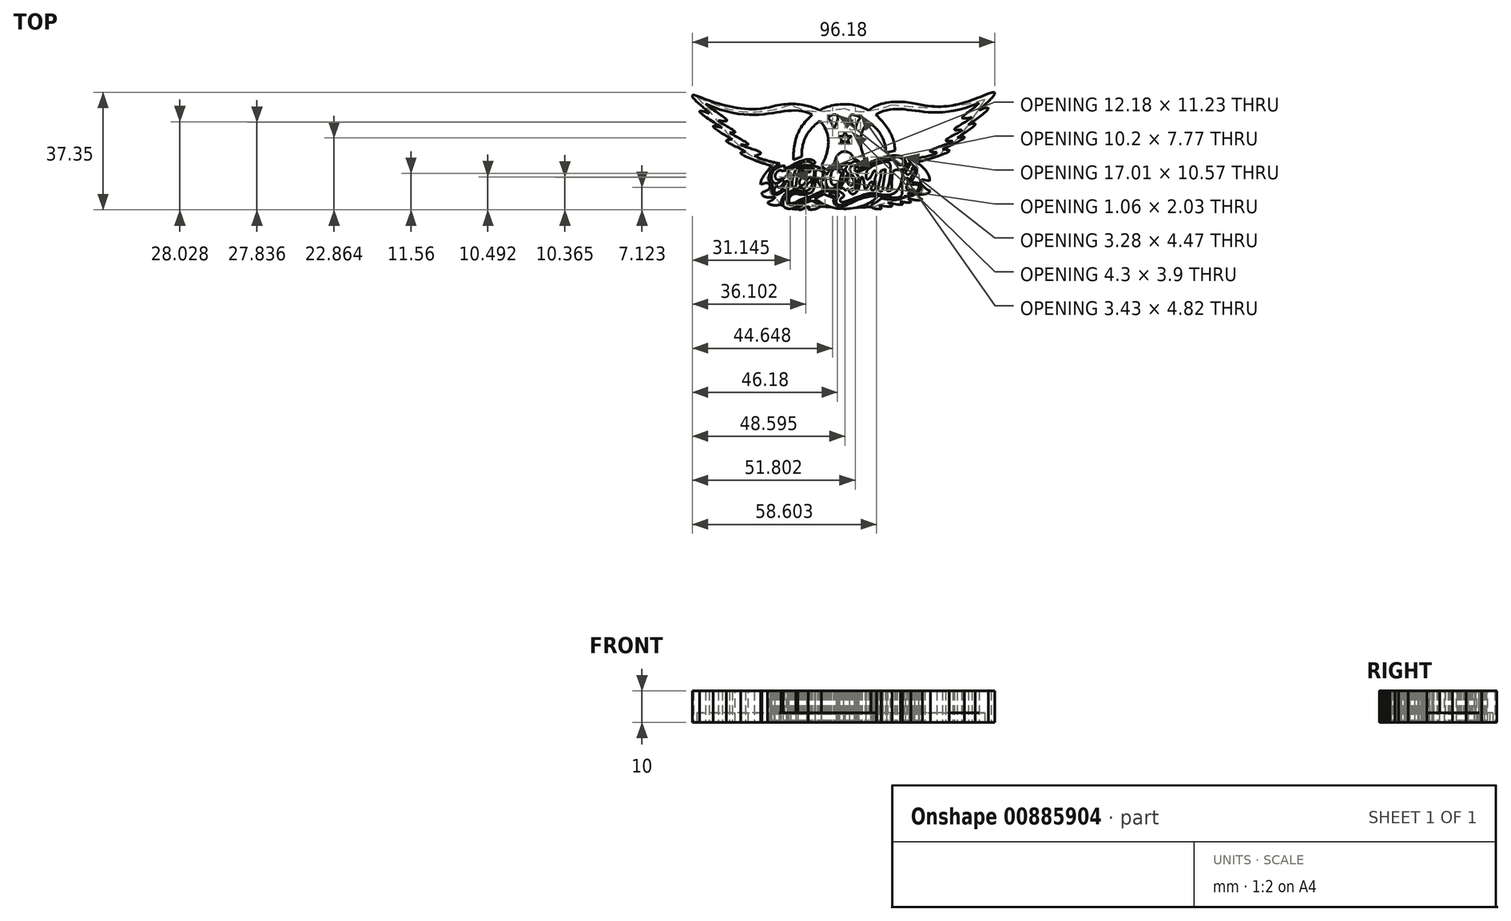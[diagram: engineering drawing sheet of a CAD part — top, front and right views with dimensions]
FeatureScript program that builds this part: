
annotation { "Feature Type Name" : "Feature", "Feature Type Description" : "" }
export const myFeature = defineFeature(function(context is Context, id is Id, definition is map)
    precondition{}
    {
        {
            var Q0;
            Q0=qCreatedBy(makeId("Top.planeOp"),FACE);
            var sketch = newSketch(context, id + "F0", { "sketchPlane" : qUnion([Q0])});
            skFitSpline(sketch, "E0", {"points": [v(7.51, 9) * mm, v(-8.16, 9) * mm], "startDerivative": vector(-19.66, 10.73) * mm, "endDerivative": vector(-7.2, -4.19) * mm});
            skFitSpline(sketch, "E1", {"points": [v(-8.16, 9) * mm, v(-22.9, 10.27) * mm], "startDerivative": vector(-8.53, 4.41) * mm, "endDerivative": vector(-19.9, -5.12) * mm});
            skFitSpline(sketch, "E2", {"points": [v(-22.9, 10.27) * mm, v(-48.15, 13.96) * mm], "startDerivative": vector(-29.2, -8.51) * mm, "endDerivative": vector(-14.66, 5.46) * mm});
            skFitSpline(sketch, "E3", {"points": [v(-10.39, 7.53) * mm, v(-44.35, 11.04) * mm], "startDerivative": vector(-25.62, 14.16) * mm, "endDerivative": vector(-54.74, 24.31) * mm});
            skFitSpline(sketch, "E4", {"points": [v(-44.35, 11.04) * mm, v(-40.28, 5.86) * mm], "startDerivative": vector(11.2, -9.7) * mm, "endDerivative": vector(-19.72, 3.9) * mm});
            skFitSpline(sketch, "E5", {"points": [v(-40.28, 5.86) * mm, v(-36.69, 1.93) * mm], "startDerivative": vector(3.4, -4.34) * mm, "endDerivative": vector(-15.17, 2.15) * mm});
            skFitSpline(sketch, "E6", {"points": [v(-36.69, 1.93) * mm, v(-33.16, -1.86) * mm], "startDerivative": vector(3.7, -3.87) * mm, "endDerivative": vector(-19.52, 3.21) * mm});
            skFitSpline(sketch, "E7", {"points": [v(-33.16, -1.86) * mm, v(-28.8, -5.45) * mm], "startDerivative": vector(2.62, -3.63) * mm, "endDerivative": vector(-18.03, -3.33) * mm});
            skFitSpline(sketch, "E8", {"points": [v(-28.8, -5.45) * mm, v(-20.78, -7.94) * mm], "startDerivative": vector(7.38, -3.87) * mm, "endDerivative": vector(8.1, -1.71) * mm});
            skFitSpline(sketch, "E9", {"points": [v(-48.15, 13.96) * mm, v(-43.13, 7.95) * mm], "startDerivative": vector(-5.71, -1.67) * mm, "endDerivative": vector(4.53, -6.24) * mm});
            skFitSpline(sketch, "E10", {"points": [v(-43.13, 7.95) * mm, v(-39.07, 3.38) * mm], "startDerivative": vector(-25.12, 9.21) * mm, "endDerivative": vector(4.95, -3.95) * mm});
            skFitSpline(sketch, "E11", {"points": [v(-39.07, 3.38) * mm, v(-35.78, -0.33) * mm], "startDerivative": vector(-22.27, 7.16) * mm, "endDerivative": vector(4.26, -2.8) * mm});
            skFitSpline(sketch, "E12", {"points": [v(-35.78, -0.33) * mm, v(-31.59, -4.23) * mm], "startDerivative": vector(-16.76, 0.42) * mm, "endDerivative": vector(4.93, -4.07) * mm});
            skFitSpline(sketch, "E13", {"points": [v(-31.59, -4.23) * mm, v(-23.3, -8.74) * mm], "startDerivative": vector(-16.72, 0.24) * mm, "endDerivative": vector(8.71, -2.57) * mm});
            skFitSpline(sketch, "E14", {"points": [v(-10.39, 7.53) * mm, v(-16.44, -6.75) * mm], "startDerivative": vector(-15.22, -12.7) * mm, "endDerivative": vector(0, -16.58) * mm});
            skFitSpline(sketch, "E15", {"points": [v(-13.68, -5.76) * mm, v(-7.94, 5.61) * mm], "startDerivative": vector(-1.22, 12.34) * mm, "endDerivative": vector(13.03, 9.02) * mm});
            skFitSpline(sketch, "E16", {"points": [v(-7.94, 5.61) * mm, v(-7.44, -8.65) * mm], "startDerivative": vector(13.51, -15.77) * mm, "endDerivative": vector(-5.4, -10.59) * mm});
            skFitSpline(sketch, "E17", {"points": [v(-7.44, -8.65) * mm, v(-5.84, -9.9) * mm], "startDerivative": vector(1.56, -1.51) * mm, "endDerivative": vector(1.8, -1.04) * mm});
            skFitSpline(sketch, "E18", {"points": [v(-5.84, -9.9) * mm, v(-3.58, -8.17) * mm], "startDerivative": vector(1.51, 2.08) * mm, "endDerivative": vector(2.41, 1.22) * mm});
            skFitSpline(sketch, "E19", {"points": [v(-3.58, -8.17) * mm, v(0, -4.07) * mm], "startDerivative": vector(1.54, 2.36) * mm, "endDerivative": vector(9.12, 0.5) * mm});
            skFitSpline(sketch, "E20", {"points": [v(-5.54, 6.83) * mm, v(-3.58, 3.13) * mm], "startDerivative": vector(3.1, -3.23) * mm, "endDerivative": vector(1.08, -3.37) * mm});
            skFitSpline(sketch, "E21", {"points": [v(-3.58, 3.13) * mm, v(-5.54, 6.83) * mm], "startDerivative": vector(5.17, 9.08) * mm, "endDerivative": vector(-13.24, -6.56) * mm});
            skLineSegment(sketch, "E22", {"start": v(-16.44, -6.75) * mm, "end": v(-13.68, -5.76) * mm});
            skLineSegment(sketch, "E23", {"start": v(0, 2.15) * mm, "end": v(-0.57, 0.72) * mm});
            skLineSegment(sketch, "E24", {"start": v(-0.57, 0.72) * mm, "end": v(-2.1, 0.72) * mm});
            skLineSegment(sketch, "E25", {"start": v(-2.1, 0.72) * mm, "end": v(-1.04, -0.23) * mm});
            skLineSegment(sketch, "E26", {"start": v(-1.04, -0.23) * mm, "end": v(-1.45, -1.68) * mm});
            skLineSegment(sketch, "E27", {"start": v(-1.45, -1.68) * mm, "end": v(0, -0.83) * mm});
            skLineSegment(sketch, "E28", {"start": v(0, 2.15) * mm, "end": v(0.57, 0.7) * mm});
            skLineSegment(sketch, "E29", {"start": v(0.57, 0.7) * mm, "end": v(2.2, 0.7) * mm});
            skLineSegment(sketch, "E30", {"start": v(2.2, 0.7) * mm, "end": v(0.91, -0.27) * mm});
            skLineSegment(sketch, "E31", {"start": v(0.91, -0.27) * mm, "end": v(1.41, -1.75) * mm});
            skLineSegment(sketch, "E32", {"start": v(1.41, -1.75) * mm, "end": v(0, -0.83) * mm});
            skFitSpline(sketch, "E33", {"points": [v(46.47, 14.61) * mm, v(42.65, 9) * mm], "startDerivative": vector(10.82, 2.12) * mm, "endDerivative": vector(-4.98, -5.73) * mm});
            skFitSpline(sketch, "E34", {"points": [v(42.65, 9) * mm, v(39.29, 4.46) * mm], "startDerivative": vector(22.47, 9) * mm, "endDerivative": vector(-5.37, -3.44) * mm});
            skFitSpline(sketch, "E35", {"points": [v(39.29, 4.46) * mm, v(35.62, 0.26) * mm], "startDerivative": vector(17.57, 5.37) * mm, "endDerivative": vector(-5.44, -3.24) * mm});
            skFitSpline(sketch, "E36", {"points": [v(35.62, 0.26) * mm, v(30.96, -3.47) * mm], "startDerivative": vector(20.25, 4.42) * mm, "endDerivative": vector(-5.56, -2.79) * mm});
            skFitSpline(sketch, "E37", {"points": [v(30.96, -3.47) * mm, v(22.69, -7.55) * mm], "startDerivative": vector(20.78, 0.18) * mm, "endDerivative": vector(-11.3, -2.83) * mm});
            skFitSpline(sketch, "E38", {"points": [v(4.97, 6.82) * mm, v(1.94, 7.58) * mm], "startDerivative": vector(-3.03, 0.94) * mm, "endDerivative": vector(-2.67, -0.27) * mm});
            skFitSpline(sketch, "E39", {"points": [v(4.97, 6.82) * mm, v(3.37, 2.77) * mm], "startDerivative": vector(-2.94, -3.79) * mm, "endDerivative": vector(-0.18, -4.9) * mm});
            skFitSpline(sketch, "E40", {"points": [v(3.37, 2.77) * mm, v(1.94, 7.58) * mm], "startDerivative": vector(-2.4, 5.16) * mm, "endDerivative": vector(3.66, 2.94) * mm});
            skFitSpline(sketch, "E41", {"points": [v(13, -4.44) * mm, v(7.46, 5.3) * mm], "startDerivative": vector(-0.68, 16.82) * mm, "endDerivative": vector(-5.72, 3.88) * mm});
            skFitSpline(sketch, "E42", {"points": [v(9.8, 7.58) * mm, v(15.93, -3.89) * mm], "startDerivative": vector(13.55, -12.82) * mm, "endDerivative": vector(0.67, -11.66) * mm});
            skFitSpline(sketch, "E43", {"points": [v(42.6, 11.32) * mm, v(9.8, 7.58) * mm], "startDerivative": vector(-51.28, -21.71) * mm, "endDerivative": vector(-26.27, -16.23) * mm});
            skFitSpline(sketch, "E44", {"points": [v(0, -4.07) * mm, v(2.9, -6.68) * mm], "startDerivative": vector(6.07, -0.78) * mm, "endDerivative": vector(1.64, -3.33) * mm});
            skFitSpline(sketch, "E45", {"points": [v(2.9, -6.68) * mm, v(4.88, -8.28) * mm], "startDerivative": vector(4.2, 0.03) * mm, "endDerivative": vector(-0.06, -1.47) * mm});
            skFitSpline(sketch, "E46", {"points": [v(4.88, -8.28) * mm, v(6.78, -7.43) * mm], "startDerivative": vector(1.83, 0.98) * mm, "endDerivative": vector(1.91, 0.75) * mm});
            skFitSpline(sketch, "E47", {"points": [v(6.78, -7.43) * mm, v(7.46, 5.3) * mm], "startDerivative": vector(-10.94, 20.01) * mm, "endDerivative": vector(4.9, 4.28) * mm});
            skLineSegment(sketch, "E48", {"start": v(13, -4.44) * mm, "end": v(15.93, -3.89) * mm});
            skFitSpline(sketch, "E49", {"points": [v(7.51, 9) * mm, v(25.36, 10.57) * mm], "startDerivative": vector(16.41, 12.57) * mm, "endDerivative": vector(12.75, -2.74) * mm});
            skFitSpline(sketch, "E50", {"points": [v(25.36, 10.57) * mm, v(46.47, 14.61) * mm], "startDerivative": vector(24.75, -4.35) * mm, "endDerivative": vector(20.92, 7.97) * mm});
            skFitSpline(sketch, "E51", {"points": [v(42.6, 11.32) * mm, v(40.38, 6.8) * mm], "startDerivative": vector(-6.33, -7.94) * mm, "endDerivative": vector(21.8, 4.75) * mm});
            skFitSpline(sketch, "E52", {"points": [v(40.38, 6.8) * mm, v(37, 2.82) * mm], "startDerivative": vector(-12.02, -9.09) * mm, "endDerivative": vector(15.26, 1.9) * mm});
            skFitSpline(sketch, "E53", {"points": [v(37, 2.82) * mm, v(34.23, -0.75) * mm], "startDerivative": vector(3.7, -1.46) * mm, "endDerivative": vector(19.81, 2.03) * mm});
            skFitSpline(sketch, "E54", {"points": [v(34.23, -0.75) * mm, v(29.18, -4.39) * mm], "startDerivative": vector(-0.7, -3.1) * mm, "endDerivative": vector(20.5, -0.32) * mm});
            skFitSpline(sketch, "E55", {"points": [v(29.18, -4.39) * mm, v(20.14, -6.67) * mm], "startDerivative": vector(-2.23, -3.48) * mm, "endDerivative": vector(-8.74, -1.5) * mm});
            skFitSpline(sketch, "E56", {"points": [v(20.14, -6.67) * mm, v(22.25, -9.08) * mm], "startDerivative": vector(1.6, -2.95) * mm, "endDerivative": vector(2.1, -2.4) * mm});
            skFitSpline(sketch, "E57", {"points": [v(22.25, -9.08) * mm, v(21.49, -13.15) * mm], "startDerivative": vector(4.95, -4.71) * mm, "endDerivative": vector(-1.52, -3.93) * mm});
            skFitSpline(sketch, "E58", {"points": [v(21.49, -13.15) * mm, v(21.94, -14.01) * mm], "startDerivative": vector(-1.73, -2.55) * mm, "endDerivative": vector(1.29, -0.2) * mm});
            skFitSpline(sketch, "E59", {"points": [v(21.94, -14.01) * mm, v(22.9, -17.43) * mm], "startDerivative": vector(10.73, -0.07) * mm, "endDerivative": vector(-3.01, -2) * mm});
            skFitSpline(sketch, "E60", {"points": [v(22.9, -17.43) * mm, v(18.96, -18.38) * mm], "startDerivative": vector(-4.08, -2.67) * mm, "endDerivative": vector(-4.05, -0.14) * mm});
            skFitSpline(sketch, "E61", {"points": [v(18.96, -18.38) * mm, v(11.27, -19.15) * mm, v(11.3, -19.26) * mm], "startDerivative": vector(-5.15, -6.8) * mm, "endDerivative": vector(0.72, 0.02) * mm});
            skFitSpline(sketch, "E62", {"points": [v(11.3, -19.26) * mm, v(8.26, -21.29) * mm], "startDerivative": vector(-2.92, -2.3) * mm, "endDerivative": vector(-3.05, -2.2) * mm});
            skFitSpline(sketch, "E63", {"points": [v(8.26, -21.29) * mm, v(9.98, -22.41) * mm], "startDerivative": vector(-0.9, -1.85) * mm, "endDerivative": vector(2.16, -0.44) * mm});
            skFitSpline(sketch, "E64", {"points": [v(9.98, -22.41) * mm, v(10.88, -21.29) * mm], "startDerivative": vector(6.54, -0.35) * mm, "endDerivative": vector(-2.08, 2.3) * mm});
            skFitSpline(sketch, "E65", {"points": [v(10.88, -21.29) * mm, v(13.54, -20.31) * mm, v(13.68, -20.36) * mm], "startDerivative": vector(26.4, -4.23) * mm, "endDerivative": vector(-0.45, -0.05) * mm});
            skFitSpline(sketch, "E66", {"points": [v(13.54, -20.31) * mm, v(17.79, -20.07) * mm], "startDerivative": vector(23.87, -5.33) * mm, "endDerivative": vector(2.87, -0.2) * mm});
            skFitSpline(sketch, "E67", {"points": [v(17.79, -20.07) * mm, v(20.1, -19.14) * mm], "startDerivative": vector(10.7, -1.73) * mm, "endDerivative": vector(-4.35, 3.45) * mm});
            skFitSpline(sketch, "E68", {"points": [v(23.03, -17.78) * mm, v(27.19, -16.66) * mm], "startDerivative": vector(4.57, 0.07) * mm, "endDerivative": vector(2.31, 3.62) * mm});
            skFitSpline(sketch, "E69", {"points": [v(27.19, -16.66) * mm, v(26.95, -13.5) * mm], "startDerivative": vector(-6.29, 1.1) * mm, "endDerivative": vector(17.2, -5.45) * mm});
            skFitSpline(sketch, "E70", {"points": [v(26.95, -13.5) * mm, v(22.69, -7.55) * mm], "startDerivative": vector(0.24, 3.65) * mm, "endDerivative": vector(-10.94, 6.97) * mm});
            skFitSpline(sketch, "E71", {"points": [v(20.1, -19.14) * mm, v(24.66, -19.43) * mm], "startDerivative": vector(0.71, 1.09) * mm, "endDerivative": vector(5.59, 2.25) * mm});
            skFitSpline(sketch, "E72", {"points": [v(24.66, -19.43) * mm, v(23.03, -17.78) * mm], "startDerivative": vector(-2.36, 1.01) * mm, "endDerivative": vector(-0.34, 1.8) * mm});
            skFitSpline(sketch, "E73", {"points": [v(10.33, -18.52) * mm, v(-9.7, -19.2) * mm], "startDerivative": vector(-9.07, -10.16) * mm, "endDerivative": vector(-22.65, 16.9) * mm});
            skLineSegment(sketch, "E74", {"start": v(-9.7, -19.2) * mm, "end": v(-6.7, -17.7) * mm});
            skLineSegment(sketch, "E75", {"start": v(-6.7, -17.7) * mm, "end": v(-3.48, -19) * mm});
            skFitSpline(sketch, "E76", {"points": [v(10.33, -18.52) * mm, v(-1.76, -21.6) * mm], "startDerivative": vector(-15.13, 3) * mm, "endDerivative": vector(-9.17, 0.4) * mm});
            skFitSpline(sketch, "E77", {"points": [v(-1.76, -21.6) * mm, v(-3.48, -19) * mm], "startDerivative": vector(-3.16, 0.59) * mm, "endDerivative": vector(2.04, 4.95) * mm});
            skFitSpline(sketch, "E78", {"points": [v(-7.54, -21.46) * mm, v(-10.67, -19.76) * mm], "startDerivative": vector(-3.15, 1.12) * mm, "endDerivative": vector(-2.4, 0.37) * mm});
            skFitSpline(sketch, "E79", {"points": [v(-11.72, -21.6) * mm, v(-11.72, -22.46) * mm], "startDerivative": vector(1.8, -1.2) * mm, "endDerivative": vector(-0.9, -0.82) * mm});
            skFitSpline(sketch, "E80", {"points": [v(-11.72, -22.46) * mm, v(-7.54, -21.46) * mm], "startDerivative": vector(5.55, -1.5) * mm, "endDerivative": vector(1.42, 1.27) * mm});
            skFitSpline(sketch, "E81", {"points": [v(-10.67, -19.76) * mm, v(-15.07, -22.26) * mm], "startDerivative": vector(-5.25, -1.2) * mm, "endDerivative": vector(-1.57, -2.1) * mm});
            skFitSpline(sketch, "E82", {"points": [v(-15.07, -22.26) * mm, v(-11.72, -21.6) * mm], "startDerivative": vector(2.02, -3.37) * mm, "endDerivative": vector(3.35, 0.65) * mm});
            skFitSpline(sketch, "E83", {"points": [v(-18.46, -17.3) * mm, v(-20.33, -20.94) * mm], "startDerivative": vector(-5.7, -3.1) * mm, "endDerivative": vector(0, -1.7) * mm});
            skFitSpline(sketch, "E84", {"points": [v(-24.67, -20.28) * mm, v(-22.2, -18.6) * mm], "startDerivative": vector(3.4, 1.1) * mm, "endDerivative": vector(1.5, 2.3) * mm});
            skFitSpline(sketch, "E85", {"points": [v(-22.2, -18.6) * mm, v(-26.47, -17.2) * mm], "startDerivative": vector(-3.5, -0.5) * mm, "endDerivative": vector(-0.3, 5.7) * mm});
            skFitSpline(sketch, "E86", {"points": [v(-26.47, -17.2) * mm, v(-23.83, -14.9) * mm], "startDerivative": vector(3, 1.6) * mm, "endDerivative": vector(-0.9, 4.4) * mm});
            skFitSpline(sketch, "E87", {"points": [v(-23.83, -14.9) * mm, v(-26.84, -14.58) * mm], "startDerivative": vector(-1.9, 4.3) * mm, "endDerivative": vector(-3.2, -0.6) * mm});
            skFitSpline(sketch, "E88", {"points": [v(-26.84, -14.58) * mm, v(-23.3, -8.74) * mm], "startDerivative": vector(0, 5.6) * mm, "endDerivative": vector(6.28, 6.78) * mm});
            skFitSpline(sketch, "E89", {"points": [v(-20.78, -7.94) * mm, v(-22.9, -14.76) * mm], "startDerivative": vector(-11.67, -6.35) * mm, "endDerivative": vector(6.2, -4.4) * mm});
            skFitSpline(sketch, "E90", {"points": [v(-22.9, -14.76) * mm, v(-19.15, -16.09) * mm], "startDerivative": vector(-4.38, -11.24) * mm, "endDerivative": vector(6.77, 8.15) * mm});
            skFitSpline(sketch, "E91", {"points": [v(-24.67, -20.28) * mm, v(-20.33, -20.94) * mm], "startDerivative": vector(3.4, -3.96) * mm, "endDerivative": vector(3.18, 0.82) * mm});
            skFitSpline(sketch, "E92", {"points": [v(-19.15, -16.09) * mm, v(-18.46, -17.3) * mm], "startDerivative": vector(0.25, -1.77) * mm, "endDerivative": vector(0.82, -0.72) * mm});
            skFitSpline(sketch, "E93", {"points": [v(-10.5, -7.87) * mm, v(-10.53, -6.77) * mm], "startDerivative": vector(2.96, -1.79) * mm, "endDerivative": vector(-4.82, 1.36) * mm});
            skFitSpline(sketch, "E94", {"points": [v(-10.53, -6.77) * mm, v(-19.15, -9.58) * mm], "startDerivative": vector(-9.82, 2.52) * mm, "endDerivative": vector(-4.52, -0.85) * mm});
            skFitSpline(sketch, "E95", {"points": [v(-19.15, -9.58) * mm, v(-19.15, -8.77) * mm], "startDerivative": vector(-0.17, 1.04) * mm, "endDerivative": vector(0.24, 1.07) * mm});
            skFitSpline(sketch, "E96", {"points": [v(-19.15, -8.77) * mm, v(-21.01, -8.99) * mm], "startDerivative": vector(0.28, 1) * mm, "endDerivative": vector(-1.83, -0.62) * mm});
            skFitSpline(sketch, "E97", {"points": [v(-21.01, -8.99) * mm, v(-22.16, -14.28) * mm], "startDerivative": vector(-11.77, -5.53) * mm, "endDerivative": vector(2.66, 0.56) * mm});
            skFitSpline(sketch, "E98", {"points": [v(-22.16, -14.28) * mm, v(-20.29, -13.42) * mm], "startDerivative": vector(2.66, 0.22) * mm, "endDerivative": vector(1.63, 1.08) * mm});
            skFitSpline(sketch, "E99", {"points": [v(-21.75, -14.88) * mm, v(-20.57, -16.8) * mm], "startDerivative": vector(-3.97, -4.7) * mm, "endDerivative": vector(6.47, 4.4) * mm});
            skFitSpline(sketch, "E100", {"points": [v(-20.29, -13.42) * mm, v(-19.5, -13.86) * mm], "startDerivative": vector(1.2, 0.99) * mm, "endDerivative": vector(-0.7, -2.4) * mm});
            skFitSpline(sketch, "E101", {"points": [v(-19.5, -13.86) * mm, v(-21.75, -14.88) * mm], "startDerivative": vector(-1.44, -4) * mm, "endDerivative": vector(-1.85, 4.18) * mm});
            skFitSpline(sketch, "E102", {"points": [v(-20.57, -16.8) * mm, v(-18.41, -13.42) * mm], "startDerivative": vector(2.69, 3) * mm, "endDerivative": vector(2.63, 2.62) * mm});
            skFitSpline(sketch, "E103", {"points": [v(-18.41, -13.42) * mm, v(-18.11, -15.61) * mm], "startDerivative": vector(0.9, -1.17) * mm, "endDerivative": vector(-1.88, -5.4) * mm});
            skFitSpline(sketch, "E104", {"points": [v(-13.08, -15.93) * mm, v(-10.93, -13.83) * mm], "startDerivative": vector(2.05, -0.21) * mm, "endDerivative": vector(3.45, -0.48) * mm});
            skFitSpline(sketch, "E105", {"points": [v(-10.93, -13.83) * mm, v(-10.78, -12.2) * mm], "startDerivative": vector(0.97, 2.14) * mm, "endDerivative": vector(-0.28, 1.04) * mm});
            skFitSpline(sketch, "E106", {"points": [v(-10.78, -12.2) * mm, v(-13.32, -14.79) * mm], "startDerivative": vector(-2.37, 0.58) * mm, "endDerivative": vector(-1.65, -1.22) * mm});
            skFitSpline(sketch, "E107", {"points": [v(-13.32, -14.79) * mm, v(-13.32, -12.15) * mm], "startDerivative": vector(-4.01, -2.35) * mm, "endDerivative": vector(5.26, 2.53) * mm});
            skFitSpline(sketch, "E108", {"points": [v(-13.32, -12.15) * mm, v(-13.16, -11.6) * mm], "startDerivative": vector(3.2, 0.27) * mm, "endDerivative": vector(-0.96, -0.04) * mm});
            skFitSpline(sketch, "E109", {"points": [v(-13.16, -11.6) * mm, v(-14.22, -11.97) * mm], "startDerivative": vector(-1.17, -0.04) * mm, "endDerivative": vector(-1.02, -0.14) * mm});
            skFitSpline(sketch, "E110", {"points": [v(-14.22, -11.97) * mm, v(-13.16, -10.2) * mm], "startDerivative": vector(-0.79, 2.76) * mm, "endDerivative": vector(1.38, 0.54) * mm});
            skFitSpline(sketch, "E111", {"points": [v(-13.16, -10.2) * mm, v(-11.61, -10.7) * mm], "startDerivative": vector(3.8, 0.84) * mm, "endDerivative": vector(0.04, -0.5) * mm});
            skFitSpline(sketch, "E112", {"points": [v(-11.35, -9.78) * mm, v(-14.41, -9.94) * mm], "startDerivative": vector(-1.68, 1.04) * mm, "endDerivative": vector(-0.26, -0.61) * mm});
            skFitSpline(sketch, "E113", {"points": [v(-11.61, -10.7) * mm, v(-11.06, -10.55) * mm], "startDerivative": vector(0.08, -0.55) * mm, "endDerivative": vector(0.1, 0.14) * mm});
            skFitSpline(sketch, "E114", {"points": [v(-11.06, -10.55) * mm, v(-11.35, -9.78) * mm], "startDerivative": vector(0.1, 0.55) * mm, "endDerivative": vector(-1.04, 0.94) * mm});
            skFitSpline(sketch, "E115", {"points": [v(-14.41, -9.94) * mm, v(-15.59, -14.92) * mm], "startDerivative": vector(-1.03, -0.1) * mm, "endDerivative": vector(-0.42, -5.06) * mm});
            skFitSpline(sketch, "E116", {"points": [v(-15.59, -14.92) * mm, v(-16.75, -15.02) * mm], "startDerivative": vector(-2.14, -3.18) * mm, "endDerivative": vector(-0.27, 1.84) * mm});
            skFitSpline(sketch, "E117", {"points": [v(-16.75, -15.02) * mm, v(-15.02, -9.42) * mm], "startDerivative": vector(-0.67, 7.08) * mm, "endDerivative": vector(3.5, 2.9) * mm});
            skFitSpline(sketch, "E118", {"points": [v(-15.02, -9.42) * mm, v(-9.82, -9.8) * mm], "startDerivative": vector(6.3, 3.04) * mm, "endDerivative": vector(1.34, -1.94) * mm});
            skFitSpline(sketch, "E119", {"points": [v(-16.9, -11.16) * mm, v(-17.46, -13.18) * mm], "startDerivative": vector(0.43, -2.32) * mm, "endDerivative": vector(-1.04, -1.18) * mm});
            skFitSpline(sketch, "E120", {"points": [v(-17.46, -13.18) * mm, v(-16.9, -11.16) * mm], "startDerivative": vector(-3.5, 3.15) * mm, "endDerivative": vector(1.47, -0.57) * mm});
            skFitSpline(sketch, "E121", {"points": [v(-10.5, -7.87) * mm, v(-15.86, -8.64) * mm], "startDerivative": vector(-5.92, 4.4) * mm, "endDerivative": vector(-3.43, -1.4) * mm});
            skFitSpline(sketch, "E122", {"points": [v(-15.86, -8.64) * mm, v(-19.82, -10.27) * mm], "startDerivative": vector(-5.9, -2.52) * mm, "endDerivative": vector(-5.6, -0.3) * mm});
            skFitSpline(sketch, "E123", {"points": [v(-19.82, -10.27) * mm, v(-20.76, -10.08) * mm], "startDerivative": vector(-1.67, -0.1) * mm, "endDerivative": vector(-1.53, -0.4) * mm});
            skFitSpline(sketch, "E124", {"points": [v(-20.76, -10.08) * mm, v(-21.22, -13.14) * mm], "startDerivative": vector(-6.2, -2.6) * mm, "endDerivative": vector(3.68, -0.05) * mm});
            skFitSpline(sketch, "E125", {"points": [v(-21.22, -13.14) * mm, v(-18.18, -11.24) * mm], "startDerivative": vector(4.78, 0.43) * mm, "endDerivative": vector(0.58, 1.37) * mm});
            skFitSpline(sketch, "E126", {"points": [v(-18.18, -11.24) * mm, v(-15.07, -8.84) * mm], "startDerivative": vector(1.6, 4.99) * mm, "endDerivative": vector(3.72, 0.55) * mm});
            skFitSpline(sketch, "E127", {"points": [v(-15.07, -8.84) * mm, v(-12.82, -8.46) * mm, v(-9.55, -8.84) * mm], "startDerivative": vector(5.77, 1.14) * mm, "endDerivative": vector(2.1, -1.17) * mm});
            skFitSpline(sketch, "E128", {"points": [v(-9.82, -9.8) * mm, v(-10.74, -15.43) * mm], "startDerivative": vector(0.57, -5.81) * mm, "endDerivative": vector(-0.89, -2.82) * mm});
            skFitSpline(sketch, "E129", {"points": [v(-10.74, -15.43) * mm, v(-14.38, -16.59) * mm], "startDerivative": vector(-2.14, -4.31) * mm, "endDerivative": vector(-2.95, 1.1) * mm});
            skFitSpline(sketch, "E130", {"points": [v(-14.38, -16.59) * mm, v(-18.15, -17.69) * mm], "startDerivative": vector(-4.6, 1) * mm, "endDerivative": vector(-3.34, -3.07) * mm});
            skFitSpline(sketch, "E131", {"points": [v(-18.15, -17.69) * mm, v(-15.64, -21.71) * mm], "startDerivative": vector(-11.89, -12.67) * mm, "endDerivative": vector(6.13, 4.67) * mm});
            skFitSpline(sketch, "E132", {"points": [v(-13.08, -15.93) * mm, v(-15.33, -15.82) * mm], "startDerivative": vector(-2, 0.42) * mm, "endDerivative": vector(-3.32, -1.62) * mm});
            skFitSpline(sketch, "E133", {"points": [v(-15.33, -15.82) * mm, v(-18.11, -15.61) * mm], "startDerivative": vector(-3.64, -1.81) * mm, "endDerivative": vector(2.23, 7.13) * mm});
            skFitSpline(sketch, "E134", {"points": [v(-9.55, -8.84) * mm, v(-5.87, -11.6) * mm], "startDerivative": vector(6.89, -0.68) * mm, "endDerivative": vector(1.05, -1.52) * mm});
            skFitSpline(sketch, "E135", {"points": [v(-9.41, -12.06) * mm, v(-11.53, -17.43) * mm], "startDerivative": vector(0.19, -11.07) * mm, "endDerivative": vector(-4.02, -0.58) * mm});
            skFitSpline(sketch, "E136", {"points": [v(-11.53, -17.43) * mm, v(-16.59, -17.25) * mm], "startDerivative": vector(-6.57, -0.34) * mm, "endDerivative": vector(-3.55, -1.55) * mm});
            skFitSpline(sketch, "E137", {"points": [v(-16.59, -17.25) * mm, v(-17.56, -21.14) * mm], "startDerivative": vector(-9.38, -4.72) * mm, "endDerivative": vector(2.34, -0.23) * mm});
            skFitSpline(sketch, "E138", {"points": [v(-17.56, -21.14) * mm, v(-14.94, -20.31) * mm], "startDerivative": vector(3.27, -0.33) * mm, "endDerivative": vector(2.34, 1.24) * mm});
            skFitSpline(sketch, "E139", {"points": [v(-14.94, -20.31) * mm, v(-6.36, -16.31) * mm], "startDerivative": vector(8.6, 4.01) * mm, "endDerivative": vector(8.84, 3.6) * mm});
            skFitSpline(sketch, "E140", {"points": [v(-15.16, -19.96) * mm, v(-17.65, -18.71) * mm], "startDerivative": vector(-2.73, -1.7) * mm, "endDerivative": vector(2.7, 8.37) * mm});
            skFitSpline(sketch, "E141", {"points": [v(-17.65, -18.71) * mm, v(-15.25, -17.53) * mm], "startDerivative": vector(2.23, 3.32) * mm, "endDerivative": vector(2.6, -0.25) * mm});
            skFitSpline(sketch, "E142", {"points": [v(-15.25, -17.53) * mm, v(-12.93, -17.85) * mm], "startDerivative": vector(2.7, -0.93) * mm, "endDerivative": vector(2.57, 0.04) * mm});
            skFitSpline(sketch, "E143", {"points": [v(-12.93, -17.85) * mm, v(-12.3, -18.52) * mm], "startDerivative": vector(3.08, -0.22) * mm, "endDerivative": vector(-0.97, -0.59) * mm});
            skFitSpline(sketch, "E144", {"points": [v(-12.3, -18.52) * mm, v(-15.16, -19.96) * mm], "startDerivative": vector(-2.44, -1.43) * mm, "endDerivative": vector(-2.3, -1.46) * mm});
            skFitSpline(sketch, "E145", {"points": [v(-9.41, -12.06) * mm, v(-8.26, -9.98) * mm], "startDerivative": vector(-0.44, 4.97) * mm, "endDerivative": vector(2.65, -0.82) * mm});
            skFitSpline(sketch, "E146", {"points": [v(-8.26, -9.98) * mm, v(-7.19, -12.25) * mm], "startDerivative": vector(3.47, -1) * mm, "endDerivative": vector(-1.32, -3.97) * mm});
            skFitSpline(sketch, "E147", {"points": [v(-7.19, -12.25) * mm, v(-8.68, -12.48) * mm], "startDerivative": vector(-1.51, -2.33) * mm, "endDerivative": vector(-1.32, 0.13) * mm});
            skFitSpline(sketch, "E148", {"points": [v(-8.68, -12.48) * mm, v(-6.36, -16.31) * mm], "startDerivative": vector(-1, -2.59) * mm, "endDerivative": vector(5.63, -3.41) * mm});
            skFitSpline(sketch, "E149", {"points": [v(-5.87, -11.6) * mm, v(-2.3, -8.7) * mm], "startDerivative": vector(2.56, 5.7) * mm, "endDerivative": vector(4.1, -0.15) * mm});
            skFitSpline(sketch, "E150", {"points": [v(-2.3, -8.7) * mm, v(-0.73, -8.1) * mm], "startDerivative": vector(1.6, -1.9) * mm, "endDerivative": vector(1.53, 0.86) * mm});
            skFitSpline(sketch, "E151", {"points": [v(-0.73, -8.1) * mm, v(1.12, -7.86) * mm], "startDerivative": vector(2.2, 1.67) * mm, "endDerivative": vector(1.4, -0.9) * mm});
            skFitSpline(sketch, "E152", {"points": [v(1.12, -7.86) * mm, v(2.6, -7.41) * mm], "startDerivative": vector(1.87, -0.94) * mm, "endDerivative": vector(1.48, 0.45) * mm});
            skFitSpline(sketch, "E153", {"points": [v(2.6, -7.41) * mm, v(4.22, -8.2) * mm], "startDerivative": vector(3.6, 1.37) * mm, "endDerivative": vector(0.39, -1.5) * mm});
            skFitSpline(sketch, "E154", {"points": [v(4.22, -8.2) * mm, v(5.47, -8.93) * mm, v(5.45, -8.93) * mm], "startDerivative": vector(-2.78, -7.24) * mm, "endDerivative": vector(-0.31, 0.05) * mm});
            skFitSpline(sketch, "E155", {"points": [v(5.47, -8.93) * mm, v(18.34, -6.05) * mm], "startDerivative": vector(14.32, 8.17) * mm, "endDerivative": vector(7.68, -5.31) * mm});
            skFitSpline(sketch, "E156", {"points": [v(18.34, -6.05) * mm, v(18.1, -9.86) * mm], "startDerivative": vector(5.3, -3.05) * mm, "endDerivative": vector(-2.61, -0.6) * mm});
            skFitSpline(sketch, "E157", {"points": [v(18.1, -9.86) * mm, v(15.72, -10.06) * mm], "startDerivative": vector(-2.37, -0.2) * mm, "endDerivative": vector(-2.5, -0.57) * mm});
            skFitSpline(sketch, "E158", {"points": [v(15.72, -10.06) * mm, v(14.81, -16.14) * mm], "startDerivative": vector(-2.84, -1.24) * mm, "endDerivative": vector(-0.22, -6.22) * mm});
            skFitSpline(sketch, "E159", {"points": [v(14.81, -16.14) * mm, v(13.32, -16.45) * mm], "startDerivative": vector(0.04, -1.54) * mm, "endDerivative": vector(0.1, 1.12) * mm});
            skFitSpline(sketch, "E160", {"points": [v(13.32, -16.45) * mm, v(14.3, -8.17) * mm], "startDerivative": vector(3.38, 9.74) * mm, "endDerivative": vector(-1.3, 5.73) * mm});
            skFitSpline(sketch, "E161", {"points": [v(14.3, -8.17) * mm, v(10.38, -8.01) * mm], "startDerivative": vector(-0.8, 3.45) * mm, "endDerivative": vector(-4.76, -1.91) * mm});
            skFitSpline(sketch, "E162", {"points": [v(10.38, -8.01) * mm, v(6.86, -10.7) * mm], "startDerivative": vector(-10.14, -4.3) * mm, "endDerivative": vector(-0.45, -1.63) * mm});
            skFitSpline(sketch, "E163", {"points": [v(6.86, -10.7) * mm, v(8.4, -11.78) * mm], "startDerivative": vector(-2.08, -9.38) * mm, "endDerivative": vector(1.85, 4.21) * mm});
            skFitSpline(sketch, "E164", {"points": [v(8.4, -11.78) * mm, v(9.29, -10.23) * mm], "startDerivative": vector(0.97, 1.72) * mm, "endDerivative": vector(0.58, -0.18) * mm});
            skFitSpline(sketch, "E165", {"points": [v(9.29, -10.23) * mm, v(9.97, -10.95) * mm], "startDerivative": vector(0.9, 0.27) * mm, "endDerivative": vector(0.2, -1.43) * mm});
            skFitSpline(sketch, "E166", {"points": [v(9.97, -10.95) * mm, v(9.52, -14.13) * mm], "startDerivative": vector(-0.06, -2.65) * mm, "endDerivative": vector(1.07, -3.55) * mm});
            skFitSpline(sketch, "E167", {"points": [v(9.52, -14.13) * mm, v(9.14, -16.44) * mm], "startDerivative": vector(1.22, -3.07) * mm, "endDerivative": vector(-1.67, -0.4) * mm});
            skFitSpline(sketch, "E168", {"points": [v(9.14, -16.44) * mm, v(8.6, -15.13) * mm], "startDerivative": vector(-3.93, -0.36) * mm, "endDerivative": vector(0.95, 2.02) * mm});
            skFitSpline(sketch, "E169", {"points": [v(8.6, -15.13) * mm, v(8.54, -13.72) * mm], "startDerivative": vector(1.86, 2.37) * mm, "endDerivative": vector(-0.5, 0.16) * mm});
            skFitSpline(sketch, "E170", {"points": [v(8.54, -13.72) * mm, v(6.36, -15.96) * mm], "startDerivative": vector(-2.34, 0.1) * mm, "endDerivative": vector(-2.65, 0.38) * mm});
            skFitSpline(sketch, "E171", {"points": [v(6.36, -15.96) * mm, v(5.47, -12.22) * mm], "startDerivative": vector(-0.64, -0.33) * mm, "endDerivative": vector(-1.7, 0.17) * mm});
            skFitSpline(sketch, "E172", {"points": [v(5.47, -12.22) * mm, v(4.32, -15.87) * mm], "startDerivative": vector(-1.98, -0.05) * mm, "endDerivative": vector(-1.18, -3) * mm});
            skFitSpline(sketch, "E173", {"points": [v(4.32, -15.87) * mm, v(1.1, -16.05) * mm], "startDerivative": vector(-1.82, -4.49) * mm, "endDerivative": vector(-2.12, 8.7) * mm});
            skFitSpline(sketch, "E174", {"points": [v(1.1, -16.05) * mm, v(0.2, -16.46) * mm], "startDerivative": vector(-1.4, 0.27) * mm, "endDerivative": vector(-0.9, -0.41) * mm});
            skFitSpline(sketch, "E175", {"points": [v(0.2, -16.46) * mm, v(-0.78, -15.7) * mm], "startDerivative": vector(-0.6, -0.4) * mm, "endDerivative": vector(-1.83, 0.74) * mm});
            skFitSpline(sketch, "E176", {"points": [v(-0.78, -15.7) * mm, v(-2.11, -16.38) * mm], "startDerivative": vector(-1.93, -0.1) * mm, "endDerivative": vector(-0.17, -0.37) * mm});
            skFitSpline(sketch, "E177", {"points": [v(-2.11, -16.38) * mm, v(-2.11, -16.74) * mm], "startDerivative": vector(-0.38, -0.66) * mm, "endDerivative": vector(0.25, -0.04) * mm});
            skFitSpline(sketch, "E178", {"points": [v(-2.11, -16.74) * mm, v(-0.92, -18.82) * mm], "startDerivative": vector(3.17, -1.08) * mm, "endDerivative": vector(-4.2, -2.39) * mm});
            skFitSpline(sketch, "E179", {"points": [v(-0.92, -18.82) * mm, v(0.2, -19.97) * mm], "startDerivative": vector(-4.72, -3.36) * mm, "endDerivative": vector(3.73, 1.65) * mm});
            skFitSpline(sketch, "E180", {"points": [v(-15.64, -21.71) * mm, v(-4.33, -16.5) * mm], "startDerivative": vector(11.98, 8.12) * mm, "endDerivative": vector(6.03, -0.22) * mm});
            skFitSpline(sketch, "E181", {"points": [v(-4.33, -16.5) * mm, v(-2.16, -18.41) * mm], "startDerivative": vector(5.54, -0.38) * mm, "endDerivative": vector(-1.53, -1.4) * mm});
            skFitSpline(sketch, "E182", {"points": [v(-2.16, -18.41) * mm, v(-1.18, -21.11) * mm], "startDerivative": vector(-5.38, -7.34) * mm, "endDerivative": vector(1.25, 0.86) * mm});
            skFitSpline(sketch, "E183", {"points": [v(-1.18, -21.11) * mm, v(8.09, -17.9) * mm], "startDerivative": vector(9.27, 3.2) * mm, "endDerivative": vector(5.69, -0.1) * mm});
            skFitSpline(sketch, "E184", {"points": [v(8.09, -17.9) * mm, v(16.3, -18.84) * mm], "startDerivative": vector(8.58, -0.5) * mm, "endDerivative": vector(8.5, -0.32) * mm});
            skFitSpline(sketch, "E185", {"points": [v(16.3, -18.84) * mm, v(18.23, -16.5) * mm], "startDerivative": vector(6.52, 0.57) * mm, "endDerivative": vector(0.34, 2.28) * mm});
            skFitSpline(sketch, "E186", {"points": [v(0.2, -19.97) * mm, v(8.5, -17.39) * mm], "startDerivative": vector(8.31, 2.58) * mm, "endDerivative": vector(5.68, -0.26) * mm});
            skFitSpline(sketch, "E187", {"points": [v(8.5, -17.39) * mm, v(15.89, -17.23) * mm], "startDerivative": vector(7.38, 0.16) * mm, "endDerivative": vector(7.82, 4.88) * mm});
            skFitSpline(sketch, "E188", {"points": [v(15.89, -17.23) * mm, v(18.37, -10.26) * mm], "startDerivative": vector(6.03, 3.99) * mm, "endDerivative": vector(-0.16, 4.44) * mm});
            skFitSpline(sketch, "E189", {"points": [v(18.23, -16.5) * mm, v(19.94, -12.63) * mm], "startDerivative": vector(0.08, 4.9) * mm, "endDerivative": vector(5.4, -1.46) * mm});
            skFitSpline(sketch, "E190", {"points": [v(19.94, -12.63) * mm, v(19.66, -14.93) * mm], "startDerivative": vector(1.51, -0.16) * mm, "endDerivative": vector(-0.87, -2.73) * mm});
            skFitSpline(sketch, "E191", {"points": [v(19.66, -14.93) * mm, v(21.27, -16.12) * mm], "startDerivative": vector(-1.1, -2) * mm, "endDerivative": vector(5.41, 2.82) * mm});
            skFitSpline(sketch, "E192", {"points": [v(21.27, -16.12) * mm, v(21.8, -16.71) * mm], "startDerivative": vector(1, 0.35) * mm, "endDerivative": vector(-1.33, -1.65) * mm});
            skFitSpline(sketch, "E193", {"points": [v(21.8, -16.71) * mm, v(19.98, -17.56) * mm], "startDerivative": vector(-1.83, -1.13) * mm, "endDerivative": vector(-1.27, -1.32) * mm});
            skFitSpline(sketch, "E194", {"points": [v(19.98, -17.56) * mm, v(23.53, -15.38) * mm], "startDerivative": vector(2.1, -0.57) * mm, "endDerivative": vector(1.3, 5.8) * mm});
            skFitSpline(sketch, "E195", {"points": [v(18.37, -10.26) * mm, v(20.02, -8) * mm], "startDerivative": vector(3.18, 1.46) * mm, "endDerivative": vector(0.91, 0.07) * mm});
            skFitSpline(sketch, "E196", {"points": [v(20.02, -8) * mm, v(20.4, -8.81) * mm], "startDerivative": vector(0.8, 0.36) * mm, "endDerivative": vector(-1.04, -1.69) * mm});
            skFitSpline(sketch, "E197", {"points": [v(20.4, -8.81) * mm, v(19.81, -11.4) * mm], "startDerivative": vector(-2.35, -3.86) * mm, "endDerivative": vector(3.34, -0.94) * mm});
            skFitSpline(sketch, "E198", {"points": [v(19.81, -11.4) * mm, v(21.41, -9.2) * mm], "startDerivative": vector(2.2, -0.84) * mm, "endDerivative": vector(0.33, 3.47) * mm});
            skFitSpline(sketch, "E199", {"points": [v(21.41, -9.2) * mm, v(22.23, -10.67) * mm], "startDerivative": vector(0.62, 0.76) * mm, "endDerivative": vector(-0.52, -1.16) * mm});
            skFitSpline(sketch, "E200", {"points": [v(22.23, -10.67) * mm, v(20.41, -13.97) * mm], "startDerivative": vector(-4.1, -4.09) * mm, "endDerivative": vector(-1.3, -3.67) * mm});
            skFitSpline(sketch, "E201", {"points": [v(20.41, -13.97) * mm, v(21.68, -14.6) * mm], "startDerivative": vector(-0.46, -2.55) * mm, "endDerivative": vector(1.22, 0.08) * mm});
            skFitSpline(sketch, "E202", {"points": [v(21.68, -14.6) * mm, v(23.53, -15.38) * mm], "startDerivative": vector(2.62, 0.36) * mm, "endDerivative": vector(-0.22, -2.34) * mm});
            skFitSpline(sketch, "E203", {"points": [v(-5.15, -17.52) * mm, v(-2.87, -18.63) * mm], "startDerivative": vector(2.02, -1.32) * mm, "endDerivative": vector(1.92, -0.59) * mm});
            skFitSpline(sketch, "E204", {"points": [v(-5.15, -17.52) * mm, v(-2.87, -18.63) * mm], "startDerivative": vector(3.3, 2.43) * mm, "endDerivative": vector(-2.45, -3.23) * mm});
            skFitSpline(sketch, "E205", {"points": [v(12.87, -9.69) * mm, v(12.1, -16) * mm], "startDerivative": vector(-0.6, -7.26) * mm, "endDerivative": vector(0.42, -4.24) * mm});
            skFitSpline(sketch, "E206", {"points": [v(12.1, -16) * mm, v(10.5, -16) * mm], "startDerivative": vector(-0.4, -3.72) * mm, "endDerivative": vector(0.11, 2.08) * mm});
            skFitSpline(sketch, "E207", {"points": [v(10.5, -16) * mm, v(11.44, -10.96) * mm], "startDerivative": vector(0.36, 5.01) * mm, "endDerivative": vector(-0.23, 5.37) * mm});
            skFitSpline(sketch, "E208", {"points": [v(11.44, -10.96) * mm, v(11.8, -10) * mm], "startDerivative": vector(-0.5, 0.5) * mm, "endDerivative": vector(2.29, 1.57) * mm});
            skFitSpline(sketch, "E209", {"points": [v(11.8, -10) * mm, v(12.87, -9.69) * mm], "startDerivative": vector(1.42, -0.19) * mm, "endDerivative": vector(1.13, 0.42) * mm});
            skFitSpline(sketch, "E210", {"points": [v(-6.15, -12.93) * mm, v(-2.63, -15.3) * mm], "startDerivative": vector(-0.07, -4.34) * mm, "endDerivative": vector(9.02, 5.01) * mm});
            skFitSpline(sketch, "E211", {"points": [v(-2.63, -15.3) * mm, v(-0.47, -10.2) * mm], "startDerivative": vector(5.88, 3.34) * mm, "endDerivative": vector(0.4, 5.48) * mm});
            skFitSpline(sketch, "E212", {"points": [v(-0.47, -10.2) * mm, v(-1.47, -9.68) * mm], "startDerivative": vector(-0.66, 1.27) * mm, "endDerivative": vector(-0.73, -0.18) * mm});
            skFitSpline(sketch, "E213", {"points": [v(-1.47, -9.68) * mm, v(-1.83, -10.68) * mm], "startDerivative": vector(-2.3, -0.66) * mm, "endDerivative": vector(0.84, -0.33) * mm});
            skFitSpline(sketch, "E214", {"points": [v(-6.15, -12.93) * mm, v(-7.42, -13.35) * mm], "startDerivative": vector(-1.27, -0.42) * mm, "endDerivative": vector(-1.55, -0.88) * mm});
            skFitSpline(sketch, "E215", {"points": [v(-7.42, -13.35) * mm, v(-5.32, -16.03) * mm], "startDerivative": vector(-1.38, -5.8) * mm, "endDerivative": vector(0.92, -0.2) * mm});
            skFitSpline(sketch, "E216", {"points": [v(-5.32, -16.03) * mm, v(-2.84, -16.03) * mm], "startDerivative": vector(2.52, -0.65) * mm, "endDerivative": vector(2.12, 0.56) * mm});
            skFitSpline(sketch, "E217", {"points": [v(-2.84, -16.03) * mm, v(-0.84, -14.67) * mm], "startDerivative": vector(2.8, 0.85) * mm, "endDerivative": vector(1.5, 1.56) * mm});
            skFitSpline(sketch, "E218", {"points": [v(-0.84, -14.67) * mm, v(-0.55, -13.93) * mm], "startDerivative": vector(0.2, 0.79) * mm, "endDerivative": vector(0.73, 0.33) * mm});
            skFitSpline(sketch, "E219", {"points": [v(-0.55, -13.93) * mm, v(0.42, -11.73) * mm], "startDerivative": vector(3.01, 1.67) * mm, "endDerivative": vector(0.55, 2.27) * mm});
            skFitSpline(sketch, "E220", {"points": [v(-1.83, -10.68) * mm, v(-1.12, -10.94) * mm], "startDerivative": vector(0.7, -0.26) * mm, "endDerivative": vector(0.7, -1.02) * mm});
            skFitSpline(sketch, "E221", {"points": [v(-1.12, -10.94) * mm, v(-3.6, -14.76) * mm], "startDerivative": vector(-0.66, -6.9) * mm, "endDerivative": vector(-4.24, 0.67) * mm});
            skFitSpline(sketch, "E222", {"points": [v(-3.6, -14.76) * mm, v(-3.33, -9.6) * mm], "startDerivative": vector(-4.05, 0.42) * mm, "endDerivative": vector(4.89, 2.17) * mm});
            skFitSpline(sketch, "E223", {"points": [v(-3.33, -9.6) * mm, v(-2.36, -9.85) * mm], "startDerivative": vector(1.23, 0.14) * mm, "endDerivative": vector(0.92, -0.52) * mm});
            skFitSpline(sketch, "E224", {"points": [v(-2.36, -9.85) * mm, v(-0.7, -8.64) * mm], "startDerivative": vector(0.67, 0.03) * mm, "endDerivative": vector(1.87, 1.37) * mm});
            skFitSpline(sketch, "E225", {"points": [v(-0.7, -8.64) * mm, v(0.27, -8.51) * mm], "startDerivative": vector(1.41, 0.73) * mm, "endDerivative": vector(0.33, -0.52) * mm});
            skFitSpline(sketch, "E226", {"points": [v(0.27, -8.51) * mm, v(0.38, -9.2) * mm], "startDerivative": vector(1.25, -0.77) * mm, "endDerivative": vector(-0.48, -0.48) * mm});
            skFitSpline(sketch, "E227", {"points": [v(0.38, -9.2) * mm, v(0.56, -10.77) * mm, v(0.56, -10.77) * mm], "startDerivative": vector(-2.02, -1.74) * mm, "endDerivative": vector(-0.13, 0.06) * mm});
            skFitSpline(sketch, "E228", {"points": [v(0.56, -10.77) * mm, v(2.72, -13.74) * mm], "startDerivative": vector(3.45, -3.07) * mm, "endDerivative": vector(-0.6, -1.92) * mm});
            skFitSpline(sketch, "E229", {"points": [v(2.72, -13.74) * mm, v(0.96, -14.25) * mm], "startDerivative": vector(0.25, -4.5) * mm, "endDerivative": vector(-0.5, 2.47) * mm});
            skFitSpline(sketch, "E230", {"points": [v(0.96, -14.25) * mm, v(0.89, -11.97) * mm], "startDerivative": vector(-1.03, 2.49) * mm, "endDerivative": vector(-0.07, 2.28) * mm});
            skFitSpline(sketch, "E231", {"points": [v(0.89, -11.97) * mm, v(0.42, -11.73) * mm], "startDerivative": vector(-0.17, 0.91) * mm, "endDerivative": vector(-0.03, -0.37) * mm});
            skFitSpline(sketch, "E232", {"points": [v(16.67, -8.22) * mm, v(18.3, -8.14) * mm], "startDerivative": vector(1.52, -0.51) * mm, "endDerivative": vector(0.8, 1.26) * mm});
            skFitSpline(sketch, "E233", {"points": [v(18.3, -8.14) * mm, v(16.67, -5.9) * mm], "startDerivative": vector(2.94, 4.63) * mm, "endDerivative": vector(-2.1, -0.2) * mm});
            skFitSpline(sketch, "E234", {"points": [v(16.67, -5.9) * mm, v(9.35, -7.5) * mm], "startDerivative": vector(-10.08, 1.34) * mm, "endDerivative": vector(-2.97, -1.4) * mm});
            skFitSpline(sketch, "E235", {"points": [v(9.35, -7.5) * mm, v(4.27, -10.23) * mm], "startDerivative": vector(-5.7, -2.64) * mm, "endDerivative": vector(-4.61, -3.09) * mm});
            skFitSpline(sketch, "E236", {"points": [v(4.27, -10.23) * mm, v(3.13, -9.67) * mm], "startDerivative": vector(-2.2, -0.99) * mm, "endDerivative": vector(1.27, 1.6) * mm});
            skFitSpline(sketch, "E237", {"points": [v(3.13, -9.67) * mm, v(2.13, -8.71) * mm], "startDerivative": vector(1.84, 4.25) * mm, "endDerivative": vector(-0.8, -0.55) * mm});
            skFitSpline(sketch, "E238", {"points": [v(2.13, -8.71) * mm, v(2.7, -12) * mm], "startDerivative": vector(-2.87, -1.8) * mm, "endDerivative": vector(3.9, -4.04) * mm});
            skFitSpline(sketch, "E239", {"points": [v(2.7, -12) * mm, v(2.85, -15.65) * mm], "startDerivative": vector(3.36, -3.96) * mm, "endDerivative": vector(-2.17, -2.52) * mm});
            skFitSpline(sketch, "E240", {"points": [v(2.85, -15.65) * mm, v(1.76, -16.08) * mm], "startDerivative": vector(-1.18, -1.39) * mm, "endDerivative": vector(-1.15, 0.18) * mm});
            skFitSpline(sketch, "E241", {"points": [v(1.76, -16.08) * mm, v(3.91, -15.3) * mm], "startDerivative": vector(1.35, -1.8) * mm, "endDerivative": vector(2.64, 3.26) * mm});
            skFitSpline(sketch, "E242", {"points": [v(3.91, -15.3) * mm, v(3.98, -11.7) * mm], "startDerivative": vector(0.49, 1.8) * mm, "endDerivative": vector(-2.5, 1.35) * mm});
            skFitSpline(sketch, "E243", {"points": [v(3.98, -11.7) * mm, v(4.66, -10.52) * mm], "startDerivative": vector(-1.1, 0.5) * mm, "endDerivative": vector(2.31, 0.91) * mm});
            skFitSpline(sketch, "E244", {"points": [v(4.66, -10.52) * mm, v(14.3, -6.72) * mm], "startDerivative": vector(9.39, 4.42) * mm, "endDerivative": vector(10.3, 0.19) * mm});
            skFitSpline(sketch, "E245", {"points": [v(14.3, -6.72) * mm, v(16.67, -8.22) * mm], "startDerivative": vector(3.54, 0.07) * mm, "endDerivative": vector(1.95, -3.39) * mm});
            skSolve(sketch);
        }
        {
            var Q0;
            Q0 = qSketchRegion(id + "F0", true);
            var Q1;
            Q1=makeQuery(id+"F0.imprint","IMPRINT",FACE,{"disambiguationData":[TD([[makeQuery(id+"F0.imprint","IMPRINT",EDGE,{"derivedFrom":sQuery(id+"F0.wireOp",EDGE,"E140")}),-1.0]])]});
            extrude(context, id + "F1", {"entities" : qUnion([Q0, Q1]), "depth" : 10 * mm, "offsetDistance" : 25 * mm});
        }
        {
            var Q0;
            Q0=qCreatedBy(makeId("Top.planeOp"),FACE);
            var sketch = newSketch(context, id + "F2", { "sketchPlane" : qUnion([Q0])});
            skFitSpline(sketch, "E246", {"points": [v(-47.19, 13.3) * mm, v(-22.56, -8.16) * mm], "startDerivative": vector(21.79, -21.79) * mm, "endDerivative": vector(32.91, -4.03) * mm});
            skFitSpline(sketch, "E247", {"points": [v(-22.56, -8.16) * mm, v(-24.74, -12.56) * mm, v(-23.93, -14.77) * mm, v(-23.87, -17.03) * mm, v(-22.86, -18.14) * mm, v(-20.98, -20.55) * mm], "startDerivative": vector(-16.58, -14.68) * mm, "endDerivative": vector(-1.66, -6.87) * mm});
            skFitSpline(sketch, "E248", {"points": [v(-20.98, -20.55) * mm, v(-15.77, -22.45) * mm, v(-13.73, -21.84) * mm, v(-4.7, -21.75) * mm, v(9.8, -21.48) * mm], "startDerivative": vector(4.33, -9.82) * mm, "endDerivative": vector(44.25, 5.8) * mm});
            skFitSpline(sketch, "E249", {"points": [v(9.8, -21.48) * mm, v(24.42, -16.87) * mm, v(23.7, -13.36) * mm, v(21.63, -7.22) * mm], "startDerivative": vector(7.22, 7.13) * mm, "endDerivative": vector(-26.96, 22.6) * mm});
            skFitSpline(sketch, "E250", {"points": [v(21.63, -7.22) * mm, v(31.06, -4.15) * mm, v(31.5, -2.98) * mm, v(34.52, -1.25) * mm, v(44.46, 12.37) * mm], "startDerivative": vector(38, 3.18) * mm, "endDerivative": vector(12.73, 19.76) * mm});
            skFitSpline(sketch, "E251", {"points": [v(44.46, 12.37) * mm, v(15.04, 10.7) * mm], "startDerivative": vector(-29.28, -8.85) * mm, "endDerivative": vector(-29.83, 4.4) * mm});
            skFitSpline(sketch, "E252", {"points": [v(15.04, 10.7) * mm, v(0, 9.47) * mm], "startDerivative": vector(-15.66, -5.52) * mm, "endDerivative": vector(-14.63, 5.79) * mm});
            skFitSpline(sketch, "E253", {"points": [v(0, 9.47) * mm, v(-17.33, 10.7) * mm], "startDerivative": vector(-16.76, -1.84) * mm, "endDerivative": vector(-21.5, 10.6) * mm});
            skFitSpline(sketch, "E254", {"points": [v(-17.33, 10.7) * mm, v(-47.19, 13.3) * mm], "startDerivative": vector(-41.77, -15.04) * mm, "endDerivative": vector(-25, 11.05) * mm});
            skSolve(sketch);
        }
        {
            var Q0;
            Q0 = qSketchRegion(id + "F2", true);
            extrude(context, id + "F3", {"entities" : qUnion([Q0]), "depth" : 3 * mm, "offsetDistance" : 25 * mm});
        }
    });
